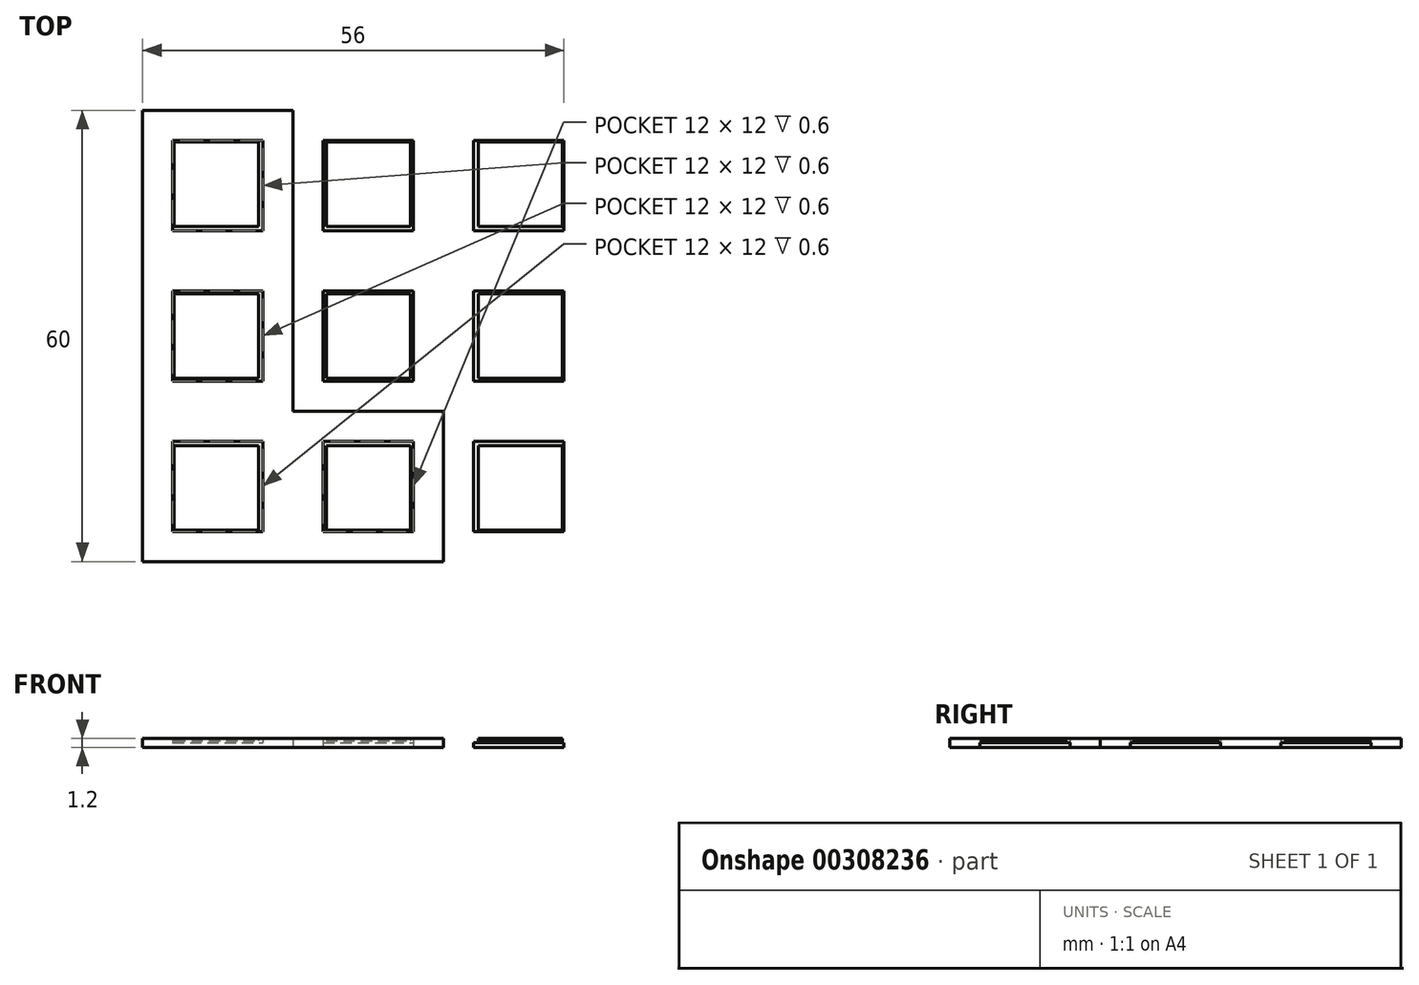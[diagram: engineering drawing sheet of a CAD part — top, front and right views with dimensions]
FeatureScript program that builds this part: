
annotation { "Feature Type Name" : "Feature", "Feature Type Description" : "" }
export const myFeature = defineFeature(function(context is Context, id is Id, definition is map)
    precondition{}
    {
        {
            var Q0;
            Q0=qCreatedBy(makeId("Top.planeOp"),FACE);
            var sketch = newSketch(context, id + "F0", { "sketchPlane" : qUnion([Q0])});
            skLineSegment(sketch, "E0.bottom", {"start": v(-10, 10) * mm, "end": v(10, 10) * mm});
            skLineSegment(sketch, "E0.top", {"start": v(-10, -10) * mm, "end": v(10, -10) * mm});
            skLineSegment(sketch, "E0.left", {"start": v(-10, 10) * mm, "end": v(-10, -10) * mm});
            skLineSegment(sketch, "E0.right", {"start": v(10, 10) * mm, "end": v(10, -10) * mm});
            skPoint(sketch, "E0.middle", {"position": v(0, 0) * mm});
            skLineSegment(sketch, "E1.bottom", {"start": v(-6, 6) * mm, "end": v(6, 6) * mm});
            skLineSegment(sketch, "E1.top", {"start": v(-6, -6) * mm, "end": v(6, -6) * mm});
            skLineSegment(sketch, "E1.left", {"start": v(-6, 6) * mm, "end": v(-6, -6) * mm});
            skLineSegment(sketch, "E1.right", {"start": v(6, 6) * mm, "end": v(6, -6) * mm});
            skLineSegment(sketch, "E2.0.1.0", {"start": v(-10, 30) * mm, "end": v(-10, 10) * mm});
            skLineSegment(sketch, "E2.0.1.1", {"start": v(-10, 30) * mm, "end": v(10, 30) * mm});
            skLineSegment(sketch, "E2.0.1.2", {"start": v(6, 26) * mm, "end": v(6, 14) * mm});
            skPoint(sketch, "E2.0.1.3", {"position": v(0, 20) * mm});
            skLineSegment(sketch, "E2.0.1.4", {"start": v(-6, 26) * mm, "end": v(6, 26) * mm});
            skLineSegment(sketch, "E2.0.1.5", {"start": v(-6, 26) * mm, "end": v(-6, 14) * mm});
            skLineSegment(sketch, "E2.0.1.7", {"start": v(-6, 14) * mm, "end": v(6, 14) * mm});
            skLineSegment(sketch, "E2.0.1.8", {"start": v(10, 30) * mm, "end": v(10, 10) * mm});
            skPoint(sketch, "E2.0.1.9", {"position": v(0, 20) * mm});
            skLineSegment(sketch, "E2.0.2.0", {"start": v(-10, 50) * mm, "end": v(-10, 30) * mm});
            skLineSegment(sketch, "E2.0.2.1", {"start": v(-10, 50) * mm, "end": v(10, 50) * mm});
            skLineSegment(sketch, "E2.0.2.2", {"start": v(6, 46) * mm, "end": v(6, 34) * mm});
            skPoint(sketch, "E2.0.2.3", {"position": v(0, 40) * mm});
            skLineSegment(sketch, "E2.0.2.4", {"start": v(-6, 46) * mm, "end": v(6, 46) * mm});
            skLineSegment(sketch, "E2.0.2.5", {"start": v(-6, 46) * mm, "end": v(-6, 34) * mm});
            skLineSegment(sketch, "E2.0.2.6", {"start": v(-10, 30) * mm, "end": v(10, 30) * mm});
            skLineSegment(sketch, "E2.0.2.7", {"start": v(-6, 34) * mm, "end": v(6, 34) * mm});
            skLineSegment(sketch, "E2.0.2.8", {"start": v(10, 50) * mm, "end": v(10, 30) * mm});
            skPoint(sketch, "E2.0.2.9", {"position": v(0, 40) * mm});
            skLineSegment(sketch, "E2.1.0.1", {"start": v(10, 10) * mm, "end": v(30, 10) * mm});
            skLineSegment(sketch, "E2.1.0.2", {"start": v(26, 6) * mm, "end": v(26, -6) * mm});
            skPoint(sketch, "E2.1.0.3", {"position": v(20, 0) * mm});
            skLineSegment(sketch, "E2.1.0.4", {"start": v(14, 6) * mm, "end": v(26, 6) * mm});
            skLineSegment(sketch, "E2.1.0.5", {"start": v(14, 6) * mm, "end": v(14, -6) * mm});
            skLineSegment(sketch, "E2.1.0.6", {"start": v(10, -10) * mm, "end": v(30, -10) * mm});
            skLineSegment(sketch, "E2.1.0.7", {"start": v(14, -6) * mm, "end": v(26, -6) * mm});
            skLineSegment(sketch, "E2.1.0.8", {"start": v(30, 10) * mm, "end": v(30, -10) * mm});
            skPoint(sketch, "E2.1.0.9", {"position": v(20, 0) * mm});
            skLineSegment(sketch, "E2.1.1.0", {"start": v(10, 30) * mm, "end": v(10, 10) * mm});
            skLineSegment(sketch, "E2.1.1.1", {"start": v(10, 30) * mm, "end": v(30, 30) * mm});
            skLineSegment(sketch, "E2.1.1.2", {"start": v(26, 26) * mm, "end": v(26, 14) * mm});
            skPoint(sketch, "E2.1.1.3", {"position": v(20, 20) * mm});
            skLineSegment(sketch, "E2.1.1.4", {"start": v(14, 26) * mm, "end": v(26, 26) * mm});
            skLineSegment(sketch, "E2.1.1.5", {"start": v(14, 26) * mm, "end": v(14, 14) * mm});
            skLineSegment(sketch, "E2.1.1.6", {"start": v(10, 10) * mm, "end": v(30, 10) * mm});
            skLineSegment(sketch, "E2.1.1.7", {"start": v(14, 14) * mm, "end": v(26, 14) * mm});
            skLineSegment(sketch, "E2.1.1.8", {"start": v(30, 30) * mm, "end": v(30, 10) * mm});
            skPoint(sketch, "E2.1.1.9", {"position": v(20, 20) * mm});
            skLineSegment(sketch, "E2.1.2.0", {"start": v(10, 50) * mm, "end": v(10, 30) * mm});
            skLineSegment(sketch, "E2.1.2.1", {"start": v(10, 50) * mm, "end": v(30, 50) * mm});
            skLineSegment(sketch, "E2.1.2.2", {"start": v(26, 46) * mm, "end": v(26, 34) * mm});
            skPoint(sketch, "E2.1.2.3", {"position": v(20, 40) * mm});
            skLineSegment(sketch, "E2.1.2.4", {"start": v(14, 46) * mm, "end": v(26, 46) * mm});
            skLineSegment(sketch, "E2.1.2.5", {"start": v(14, 46) * mm, "end": v(14, 34) * mm});
            skLineSegment(sketch, "E2.1.2.6", {"start": v(10, 30) * mm, "end": v(30, 30) * mm});
            skLineSegment(sketch, "E2.1.2.7", {"start": v(14, 34) * mm, "end": v(26, 34) * mm});
            skLineSegment(sketch, "E2.1.2.8", {"start": v(30, 50) * mm, "end": v(30, 30) * mm});
            skPoint(sketch, "E2.1.2.9", {"position": v(20, 40) * mm});
            skLineSegment(sketch, "E2.2.0.0", {"start": v(30, 10) * mm, "end": v(30, -10) * mm});
            skLineSegment(sketch, "E2.2.0.1", {"start": v(30, 10) * mm, "end": v(50, 10) * mm});
            skLineSegment(sketch, "E2.2.0.2", {"start": v(46, 6) * mm, "end": v(46, -6) * mm});
            skPoint(sketch, "E2.2.0.3", {"position": v(40, 0) * mm});
            skLineSegment(sketch, "E2.2.0.4", {"start": v(34, 6) * mm, "end": v(46, 6) * mm});
            skLineSegment(sketch, "E2.2.0.5", {"start": v(34, 6) * mm, "end": v(34, -6) * mm});
            skLineSegment(sketch, "E2.2.0.6", {"start": v(30, -10) * mm, "end": v(50, -10) * mm});
            skLineSegment(sketch, "E2.2.0.7", {"start": v(34, -6) * mm, "end": v(46, -6) * mm});
            skLineSegment(sketch, "E2.2.0.8", {"start": v(50, 10) * mm, "end": v(50, -10) * mm});
            skPoint(sketch, "E2.2.0.9", {"position": v(40, 0) * mm});
            skLineSegment(sketch, "E2.2.1.0", {"start": v(30, 30) * mm, "end": v(30, 10) * mm});
            skLineSegment(sketch, "E2.2.1.1", {"start": v(30, 30) * mm, "end": v(50, 30) * mm});
            skLineSegment(sketch, "E2.2.1.2", {"start": v(46, 26) * mm, "end": v(46, 14) * mm});
            skPoint(sketch, "E2.2.1.3", {"position": v(40, 20) * mm});
            skLineSegment(sketch, "E2.2.1.4", {"start": v(34, 26) * mm, "end": v(46, 26) * mm});
            skLineSegment(sketch, "E2.2.1.5", {"start": v(34, 26) * mm, "end": v(34, 14) * mm});
            skLineSegment(sketch, "E2.2.1.6", {"start": v(30, 10) * mm, "end": v(50, 10) * mm});
            skLineSegment(sketch, "E2.2.1.7", {"start": v(34, 14) * mm, "end": v(46, 14) * mm});
            skLineSegment(sketch, "E2.2.1.8", {"start": v(50, 30) * mm, "end": v(50, 10) * mm});
            skPoint(sketch, "E2.2.1.9", {"position": v(40, 20) * mm});
            skLineSegment(sketch, "E2.2.2.0", {"start": v(30, 50) * mm, "end": v(30, 30) * mm});
            skLineSegment(sketch, "E2.2.2.1", {"start": v(30, 50) * mm, "end": v(50, 50) * mm});
            skLineSegment(sketch, "E2.2.2.2", {"start": v(46, 46) * mm, "end": v(46, 34) * mm});
            skPoint(sketch, "E2.2.2.3", {"position": v(40, 40) * mm});
            skLineSegment(sketch, "E2.2.2.4", {"start": v(34, 46) * mm, "end": v(46, 46) * mm});
            skLineSegment(sketch, "E2.2.2.5", {"start": v(34, 46) * mm, "end": v(34, 34) * mm});
            skLineSegment(sketch, "E2.2.2.6", {"start": v(30, 30) * mm, "end": v(50, 30) * mm});
            skLineSegment(sketch, "E2.2.2.7", {"start": v(34, 34) * mm, "end": v(46, 34) * mm});
            skLineSegment(sketch, "E2.2.2.8", {"start": v(50, 50) * mm, "end": v(50, 30) * mm});
            skPoint(sketch, "E2.2.2.9", {"position": v(40, 40) * mm});
            skLineSegment(sketch, "E2.direction1", {"start": v(-10, -10) * mm, "end": v(10, -10) * mm, "construction": true});
            skLineSegment(sketch, "E2.direction2", {"start": v(-10, -10) * mm, "end": v(-10, 10) * mm, "construction": true});
            skLineSegment(sketch, "E3.bottom", {"start": v(-5.8, 45.8) * mm, "end": v(5.4, 45.8) * mm});
            skLineSegment(sketch, "E3.top", {"start": v(-5.8, 34.6) * mm, "end": v(5.4, 34.6) * mm});
            skLineSegment(sketch, "E3.left", {"start": v(-5.8, 45.8) * mm, "end": v(-5.8, 34.6) * mm});
            skLineSegment(sketch, "E3.right", {"start": v(5.4, 45.8) * mm, "end": v(5.4, 34.6) * mm});
            skLineSegment(sketch, "E4.bottom", {"start": v(14.4, 45.8) * mm, "end": v(25.6, 45.8) * mm});
            skLineSegment(sketch, "E4.top", {"start": v(14.4, 34.6) * mm, "end": v(25.6, 34.6) * mm});
            skLineSegment(sketch, "E4.left", {"start": v(14.4, 45.8) * mm, "end": v(14.4, 34.6) * mm});
            skLineSegment(sketch, "E4.right", {"start": v(25.6, 45.8) * mm, "end": v(25.6, 34.6) * mm});
            skLineSegment(sketch, "E5.bottom", {"start": v(34.6, 45.8) * mm, "end": v(45.8, 45.8) * mm});
            skLineSegment(sketch, "E5.top", {"start": v(34.6, 34.6) * mm, "end": v(45.8, 34.6) * mm});
            skLineSegment(sketch, "E5.left", {"start": v(34.6, 45.8) * mm, "end": v(34.6, 34.6) * mm});
            skLineSegment(sketch, "E5.right", {"start": v(45.8, 45.8) * mm, "end": v(45.8, 34.6) * mm});
            skLineSegment(sketch, "E6.bottom", {"start": v(34.6, 25.6) * mm, "end": v(45.8, 25.6) * mm});
            skLineSegment(sketch, "E6.top", {"start": v(34.6, 14.4) * mm, "end": v(45.8, 14.4) * mm});
            skLineSegment(sketch, "E6.left", {"start": v(34.6, 25.6) * mm, "end": v(34.6, 14.4) * mm});
            skLineSegment(sketch, "E6.right", {"start": v(45.8, 25.6) * mm, "end": v(45.8, 14.4) * mm});
            skLineSegment(sketch, "E7.bottom", {"start": v(14.4, 25.6) * mm, "end": v(25.6, 25.6) * mm});
            skLineSegment(sketch, "E7.top", {"start": v(14.4, 14.4) * mm, "end": v(25.6, 14.4) * mm});
            skLineSegment(sketch, "E7.left", {"start": v(14.4, 25.6) * mm, "end": v(14.4, 14.4) * mm});
            skLineSegment(sketch, "E7.right", {"start": v(25.6, 25.6) * mm, "end": v(25.6, 14.4) * mm});
            skLineSegment(sketch, "E8.bottom", {"start": v(-5.8, 25.6) * mm, "end": v(5.4, 25.6) * mm});
            skLineSegment(sketch, "E8.top", {"start": v(-5.8, 14.4) * mm, "end": v(5.4, 14.4) * mm});
            skLineSegment(sketch, "E8.left", {"start": v(-5.8, 25.6) * mm, "end": v(-5.8, 14.4) * mm});
            skLineSegment(sketch, "E8.right", {"start": v(5.4, 25.6) * mm, "end": v(5.4, 14.4) * mm});
            skLineSegment(sketch, "E9.bottom", {"start": v(-5.8, 5.4) * mm, "end": v(5.4, 5.4) * mm});
            skLineSegment(sketch, "E9.top", {"start": v(-5.8, -5.8) * mm, "end": v(5.4, -5.8) * mm});
            skLineSegment(sketch, "E9.left", {"start": v(-5.8, 5.4) * mm, "end": v(-5.8, -5.8) * mm});
            skLineSegment(sketch, "E9.right", {"start": v(5.4, 5.4) * mm, "end": v(5.4, -5.8) * mm});
            skLineSegment(sketch, "E10.bottom", {"start": v(14.4, 5.4) * mm, "end": v(25.6, 5.4) * mm});
            skLineSegment(sketch, "E10.top", {"start": v(14.4, -5.8) * mm, "end": v(25.6, -5.8) * mm});
            skLineSegment(sketch, "E10.left", {"start": v(14.4, 5.4) * mm, "end": v(14.4, -5.8) * mm});
            skLineSegment(sketch, "E10.right", {"start": v(25.6, 5.4) * mm, "end": v(25.6, -5.8) * mm});
            skLineSegment(sketch, "E11.bottom", {"start": v(34.6, 5.4) * mm, "end": v(45.8, 5.4) * mm});
            skLineSegment(sketch, "E11.top", {"start": v(34.6, -5.8) * mm, "end": v(45.8, -5.8) * mm});
            skLineSegment(sketch, "E11.left", {"start": v(34.6, 5.4) * mm, "end": v(34.6, -5.8) * mm});
            skLineSegment(sketch, "E11.right", {"start": v(45.8, 5.4) * mm, "end": v(45.8, -5.8) * mm});
            skSolve(sketch);
        }
        {
            var Q0;
            Q0=makeQuery(id+"F0.imprint","IMPRINT",FACE,{"disambiguationData":[TD([[makeQuery(id+"F0.imprint","IMPRINT",EDGE,{"derivedFrom":sQuery(id+"F0.wireOp",EDGE,"E3.bottom")}),-1.0]])]});
            var Q1;
            Q1=makeQuery(id+"F0.imprint","IMPRINT",FACE,{"disambiguationData":[TD([[makeQuery(id+"F0.imprint","IMPRINT",EDGE,{"derivedFrom":sQuery(id+"F0.wireOp",EDGE,"E4.bottom")}),-1.0]])]});
            var Q2;
            Q2=makeQuery(id+"F0.imprint","IMPRINT",FACE,{"disambiguationData":[TD([[makeQuery(id+"F0.imprint","IMPRINT",EDGE,{"derivedFrom":sQuery(id+"F0.wireOp",EDGE,"E5.bottom")}),-1.0]])]});
            var Q3;
            Q3=makeQuery(id+"F0.imprint","IMPRINT",FACE,{"disambiguationData":[TD([[makeQuery(id+"F0.imprint","IMPRINT",EDGE,{"derivedFrom":sQuery(id+"F0.wireOp",EDGE,"E6.bottom")}),-1.0]])]});
            var Q4;
            Q4=makeQuery(id+"F0.imprint","IMPRINT",FACE,{"disambiguationData":[TD([[makeQuery(id+"F0.imprint","IMPRINT",EDGE,{"derivedFrom":sQuery(id+"F0.wireOp",EDGE,"E7.bottom")}),-1.0]])]});
            var Q5;
            Q5=makeQuery(id+"F0.imprint","IMPRINT",FACE,{"disambiguationData":[TD([[makeQuery(id+"F0.imprint","IMPRINT",EDGE,{"derivedFrom":sQuery(id+"F0.wireOp",EDGE,"E8.bottom")}),-1.0]])]});
            var Q6;
            Q6=makeQuery(id+"F0.imprint","IMPRINT",FACE,{"disambiguationData":[TD([[makeQuery(id+"F0.imprint","IMPRINT",EDGE,{"derivedFrom":sQuery(id+"F0.wireOp",EDGE,"E9.bottom")}),-1.0]])]});
            var Q7;
            Q7=makeQuery(id+"F0.imprint","IMPRINT",FACE,{"disambiguationData":[TD([[makeQuery(id+"F0.imprint","IMPRINT",EDGE,{"derivedFrom":sQuery(id+"F0.wireOp",EDGE,"E10.bottom")}),-1.0]])]});
            var Q8;
            Q8=makeQuery(id+"F0.imprint","IMPRINT",FACE,{"disambiguationData":[TD([[makeQuery(id+"F0.imprint","IMPRINT",EDGE,{"derivedFrom":sQuery(id+"F0.wireOp",EDGE,"E11.bottom")}),-1.0]])]});
            extrude(context, id + "F1", {"entities" : qUnion([Q0, Q1, Q2, Q3, Q4, Q5, Q6, Q7, Q8]), "depth" : 1.2 * mm, "offsetDistance" : 25 * mm});
        }
        {
            var Q0;
            Q0=makeQuery(id+"F0.imprint","IMPRINT",FACE,{"disambiguationData":[TD([[makeQuery(id+"F0.imprint","IMPRINT",EDGE,{"derivedFrom":sQuery(id+"F0.wireOp",EDGE,"E9.bottom")}),-1.0]])]});
            var Q1;
            Q1=makeQuery(id+"F0.imprint","IMPRINT",FACE,{"disambiguationData":[TD([[makeQuery(id+"F0.imprint","IMPRINT",EDGE,{"derivedFrom":sQuery(id+"F0.wireOp",EDGE,"E10.bottom")}),-1.0]])]});
            var Q2;
            Q2=makeQuery(id+"F0.imprint","IMPRINT",FACE,{"disambiguationData":[TD([[makeQuery(id+"F0.imprint","IMPRINT",EDGE,{"derivedFrom":sQuery(id+"F0.wireOp",EDGE,"E11.bottom")}),-1.0]])]});
            var Q3;
            Q3=makeQuery(id+"F0.imprint","IMPRINT",FACE,{"disambiguationData":[TD([[makeQuery(id+"F0.imprint","IMPRINT",EDGE,{"derivedFrom":sQuery(id+"F0.wireOp",EDGE,"E8.bottom")}),-1.0]])]});
            var Q4;
            Q4=makeQuery(id+"F0.imprint","IMPRINT",FACE,{"disambiguationData":[TD([[makeQuery(id+"F0.imprint","IMPRINT",EDGE,{"derivedFrom":sQuery(id+"F0.wireOp",EDGE,"E7.bottom")}),-1.0]])]});
            var Q5;
            Q5=makeQuery(id+"F0.imprint","IMPRINT",FACE,{"disambiguationData":[TD([[makeQuery(id+"F0.imprint","IMPRINT",EDGE,{"derivedFrom":sQuery(id+"F0.wireOp",EDGE,"E6.bottom")}),-1.0]])]});
            var Q6;
            Q6=makeQuery(id+"F0.imprint","IMPRINT",FACE,{"disambiguationData":[TD([[makeQuery(id+"F0.imprint","IMPRINT",EDGE,{"derivedFrom":sQuery(id+"F0.wireOp",EDGE,"E3.bottom")}),-1.0]])]});
            var Q7;
            Q7=makeQuery(id+"F0.imprint","IMPRINT",FACE,{"disambiguationData":[TD([[makeQuery(id+"F0.imprint","IMPRINT",EDGE,{"derivedFrom":sQuery(id+"F0.wireOp",EDGE,"E4.bottom")}),-1.0]])]});
            var Q8;
            Q8=makeQuery(id+"F0.imprint","IMPRINT",FACE,{"disambiguationData":[TD([[makeQuery(id+"F0.imprint","IMPRINT",EDGE,{"derivedFrom":sQuery(id+"F0.wireOp",EDGE,"E5.bottom")}),-1.0]])]});
            extrude(context, id + "F2", {"entities" : qUnion([Q0, Q1, Q2, Q3, Q4, Q5, Q6, Q7, Q8]), "operationType" : NewBodyOperationType.REMOVE, "depth" : .9 * mm, "offsetDistance" : 25 * mm});
        }
        {
            var Q0;
            Q0=makeQuery(id+"F0.imprint","IMPRINT",FACE,{"disambiguationData":[TD([[makeQuery(id+"F0.imprint","IMPRINT",EDGE,{"derivedFrom":sQuery(id+"F0.wireOp",EDGE,"E2.0.2.0")}),1.0]])]});
            var Q1;
            Q1=makeQuery(id+"F0.imprint","IMPRINT",FACE,{"disambiguationData":[TD([[makeQuery(id+"F0.imprint","IMPRINT",EDGE,{"derivedFrom":sQuery(id+"F0.wireOp",EDGE,"E2.1.2.0")}),1.0]])]});
            var Q2;
            Q2=makeQuery(id+"F0.imprint","IMPRINT",FACE,{"disambiguationData":[TD([[makeQuery(id+"F0.imprint","IMPRINT",EDGE,{"derivedFrom":sQuery(id+"F0.wireOp",EDGE,"E2.2.2.0")}),1.0]])]});
            var Q3;
            Q3=makeQuery(id+"F0.imprint","IMPRINT",FACE,{"disambiguationData":[TD([[makeQuery(id+"F0.imprint","IMPRINT",EDGE,{"derivedFrom":sQuery(id+"F0.wireOp",EDGE,"E2.2.1.0")}),1.0]])]});
            var Q4;
            Q4=makeQuery(id+"F0.imprint","IMPRINT",FACE,{"disambiguationData":[TD([[makeQuery(id+"F0.imprint","IMPRINT",EDGE,{"derivedFrom":sQuery(id+"F0.wireOp",EDGE,"E2.1.1.0")}),1.0]])]});
            var Q5;
            Q5=makeQuery(id+"F0.imprint","IMPRINT",FACE,{"disambiguationData":[TD([[makeQuery(id+"F0.imprint","IMPRINT",EDGE,{"derivedFrom":sQuery(id+"F0.wireOp",EDGE,"E2.0.1.0")}),1.0]])]});
            var Q6;
            Q6=makeQuery(id+"F0.imprint","IMPRINT",FACE,{"disambiguationData":[TD([[makeQuery(id+"F0.imprint","IMPRINT",EDGE,{"derivedFrom":sQuery(id+"F0.wireOp",EDGE,"E0.top")}),1.0]])]});
            var Q7;
            Q7=makeQuery(id+"F0.imprint","IMPRINT",FACE,{"disambiguationData":[TD([[makeQuery(id+"F0.imprint","IMPRINT",EDGE,{"derivedFrom":sQuery(id+"F0.wireOp",EDGE,"E0.right")}),1.0]])]});
            var Q8;
            Q8=makeQuery(id+"F0.imprint","IMPRINT",FACE,{"disambiguationData":[TD([[makeQuery(id+"F0.imprint","IMPRINT",EDGE,{"derivedFrom":sQuery(id+"F0.wireOp",EDGE,"E2.2.0.0")}),1.0]])]});
            extrude(context, id + "F3", {"entities" : qUnion([Q0, Q1, Q2, Q3, Q4, Q5, Q6, Q7, Q8]), "depth" : 1.2 * mm, "offsetDistance" : 25 * mm});
        }
        {
            var Q0;
            Q0=makeQuery(id+"F0.imprint","IMPRINT",FACE,{"disambiguationData":[TD([[makeQuery(id+"F0.imprint","IMPRINT",EDGE,{"derivedFrom":sQuery(id+"F0.wireOp",EDGE,"E2.2.2.0")}),1.0]])]});
            var Q1;
            Q1=makeQuery(id+"F0.imprint","IMPRINT",FACE,{"disambiguationData":[TD([[makeQuery(id+"F0.imprint","IMPRINT",EDGE,{"derivedFrom":sQuery(id+"F0.wireOp",EDGE,"E5.bottom")}),-1.0]])]});
            var Q2;
            Q2=makeQuery(id+"F0.imprint","IMPRINT",FACE,{"disambiguationData":[TD([[makeQuery(id+"F0.imprint","IMPRINT",EDGE,{"derivedFrom":sQuery(id+"F0.wireOp",EDGE,"E2.2.2.2")}),-1.0]])]});
            var Q3;
            Q3=makeQuery(id+"F0.imprint","IMPRINT",FACE,{"disambiguationData":[TD([[makeQuery(id+"F0.imprint","IMPRINT",EDGE,{"derivedFrom":sQuery(id+"F0.wireOp",EDGE,"E2.2.1.0")}),1.0]])]});
            var Q4;
            Q4=makeQuery(id+"F0.imprint","IMPRINT",FACE,{"disambiguationData":[TD([[makeQuery(id+"F0.imprint","IMPRINT",EDGE,{"derivedFrom":sQuery(id+"F0.wireOp",EDGE,"E6.bottom")}),-1.0]])]});
            var Q5;
            Q5=makeQuery(id+"F0.imprint","IMPRINT",FACE,{"disambiguationData":[TD([[makeQuery(id+"F0.imprint","IMPRINT",EDGE,{"derivedFrom":sQuery(id+"F0.wireOp",EDGE,"E2.2.1.2")}),-1.0]])]});
            var Q6;
            Q6=makeQuery(id+"F0.imprint","IMPRINT",FACE,{"disambiguationData":[TD([[makeQuery(id+"F0.imprint","IMPRINT",EDGE,{"derivedFrom":sQuery(id+"F0.wireOp",EDGE,"E2.2.0.0")}),1.0]])]});
            var Q7;
            Q7=makeQuery(id+"F0.imprint","IMPRINT",FACE,{"disambiguationData":[TD([[makeQuery(id+"F0.imprint","IMPRINT",EDGE,{"derivedFrom":sQuery(id+"F0.wireOp",EDGE,"E0.right")}),1.0]])]});
            var Q8;
            Q8=makeQuery(id+"F0.imprint","IMPRINT",FACE,{"disambiguationData":[TD([[makeQuery(id+"F0.imprint","IMPRINT",EDGE,{"derivedFrom":sQuery(id+"F0.wireOp",EDGE,"E2.1.1.0")}),1.0]])]});
            var Q9;
            Q9=makeQuery(id+"F0.imprint","IMPRINT",FACE,{"disambiguationData":[TD([[makeQuery(id+"F0.imprint","IMPRINT",EDGE,{"derivedFrom":sQuery(id+"F0.wireOp",EDGE,"E2.1.2.0")}),1.0]])]});
            var Q10;
            Q10=makeQuery(id+"F0.imprint","IMPRINT",FACE,{"disambiguationData":[TD([[makeQuery(id+"F0.imprint","IMPRINT",EDGE,{"derivedFrom":sQuery(id+"F0.wireOp",EDGE,"E2.0.2.0")}),1.0]])]});
            var Q11;
            Q11=makeQuery(id+"F0.imprint","IMPRINT",FACE,{"disambiguationData":[TD([[makeQuery(id+"F0.imprint","IMPRINT",EDGE,{"derivedFrom":sQuery(id+"F0.wireOp",EDGE,"E2.0.1.0")}),1.0]])]});
            var Q12;
            Q12=makeQuery(id+"F0.imprint","IMPRINT",FACE,{"disambiguationData":[TD([[makeQuery(id+"F0.imprint","IMPRINT",EDGE,{"derivedFrom":sQuery(id+"F0.wireOp",EDGE,"E0.top")}),1.0]])]});
            var Q13;
            Q13=makeQuery(id+"F0.imprint","IMPRINT",FACE,{"disambiguationData":[TD([[makeQuery(id+"F0.imprint","IMPRINT",EDGE,{"derivedFrom":sQuery(id+"F0.wireOp",EDGE,"E9.bottom")}),-1.0]])]});
            var Q14;
            Q14=makeQuery(id+"F0.imprint","IMPRINT",FACE,{"disambiguationData":[TD([[makeQuery(id+"F0.imprint","IMPRINT",EDGE,{"derivedFrom":sQuery(id+"F0.wireOp",EDGE,"E10.bottom")}),-1.0]])]});
            var Q15;
            Q15=makeQuery(id+"F0.imprint","IMPRINT",FACE,{"disambiguationData":[TD([[makeQuery(id+"F0.imprint","IMPRINT",EDGE,{"derivedFrom":sQuery(id+"F0.wireOp",EDGE,"E11.bottom")}),-1.0]])]});
            var Q16;
            Q16=makeQuery(id+"F0.imprint","IMPRINT",FACE,{"disambiguationData":[TD([[makeQuery(id+"F0.imprint","IMPRINT",EDGE,{"derivedFrom":sQuery(id+"F0.wireOp",EDGE,"E7.bottom")}),-1.0]])]});
            var Q17;
            Q17=makeQuery(id+"F0.imprint","IMPRINT",FACE,{"disambiguationData":[TD([[makeQuery(id+"F0.imprint","IMPRINT",EDGE,{"derivedFrom":sQuery(id+"F0.wireOp",EDGE,"E4.bottom")}),-1.0]])]});
            var Q18;
            Q18=makeQuery(id+"F0.imprint","IMPRINT",FACE,{"disambiguationData":[TD([[makeQuery(id+"F0.imprint","IMPRINT",EDGE,{"derivedFrom":sQuery(id+"F0.wireOp",EDGE,"E8.bottom")}),-1.0]])]});
            var Q19;
            Q19=makeQuery(id+"F0.imprint","IMPRINT",FACE,{"disambiguationData":[TD([[makeQuery(id+"F0.imprint","IMPRINT",EDGE,{"derivedFrom":sQuery(id+"F0.wireOp",EDGE,"E3.bottom")}),-1.0]])]});
            var Q20;
            Q20=makeQuery(id+"F0.imprint","IMPRINT",FACE,{"disambiguationData":[TD([[makeQuery(id+"F0.imprint","IMPRINT",EDGE,{"derivedFrom":sQuery(id+"F0.wireOp",EDGE,"E2.0.2.2")}),-1.0]])]});
            var Q21;
            Q21=makeQuery(id+"F0.imprint","IMPRINT",FACE,{"disambiguationData":[TD([[makeQuery(id+"F0.imprint","IMPRINT",EDGE,{"derivedFrom":sQuery(id+"F0.wireOp",EDGE,"E2.1.2.2")}),-1.0]])]});
            var Q22;
            Q22=makeQuery(id+"F0.imprint","IMPRINT",FACE,{"disambiguationData":[TD([[makeQuery(id+"F0.imprint","IMPRINT",EDGE,{"derivedFrom":sQuery(id+"F0.wireOp",EDGE,"E2.1.1.2")}),-1.0]])]});
            var Q23;
            Q23=makeQuery(id+"F0.imprint","IMPRINT",FACE,{"disambiguationData":[TD([[makeQuery(id+"F0.imprint","IMPRINT",EDGE,{"derivedFrom":sQuery(id+"F0.wireOp",EDGE,"E2.0.1.2")}),-1.0]])]});
            var Q24;
            Q24=makeQuery(id+"F0.imprint","IMPRINT",FACE,{"disambiguationData":[TD([[makeQuery(id+"F0.imprint","IMPRINT",EDGE,{"derivedFrom":sQuery(id+"F0.wireOp",EDGE,"E1.bottom")}),-1.0]])]});
            var Q25;
            Q25=makeQuery(id+"F0.imprint","IMPRINT",FACE,{"disambiguationData":[TD([[makeQuery(id+"F0.imprint","IMPRINT",EDGE,{"derivedFrom":sQuery(id+"F0.wireOp",EDGE,"E2.1.0.2")}),-1.0]])]});
            var Q26;
            Q26=makeQuery(id+"F0.imprint","IMPRINT",FACE,{"disambiguationData":[TD([[makeQuery(id+"F0.imprint","IMPRINT",EDGE,{"derivedFrom":sQuery(id+"F0.wireOp",EDGE,"E2.2.0.2")}),-1.0]])]});
            extrude(context, id + "F4", {"entities" : qUnion([Q0, Q1, Q2, Q3, Q4, Q5, Q6, Q7, Q8, Q9, Q10, Q11, Q12, Q13, Q14, Q15, Q16, Q17, Q18, Q19, Q20, Q21, Q22, Q23, Q24, Q25, Q26]), "operationType" : NewBodyOperationType.ADD, "depth" : .6 * mm, "offsetDistance" : 25 * mm});
        }
    });
